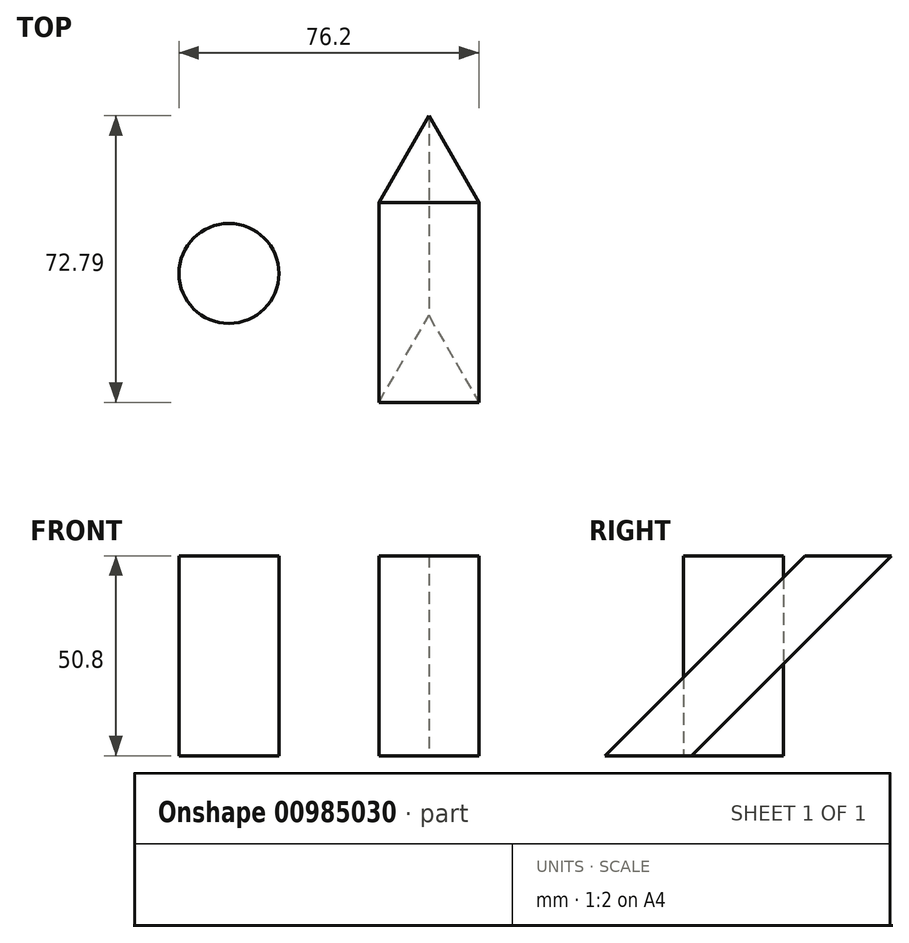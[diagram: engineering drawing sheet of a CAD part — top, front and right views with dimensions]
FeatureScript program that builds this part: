
annotation { "Feature Type Name" : "Feature", "Feature Type Description" : "" }
export const myFeature = defineFeature(function(context is Context, id is Id, definition is map)
    precondition{}
    {
        {
            var Q0;
            Q0=qCreatedBy(makeId("Top.planeOp"),FACE);
            var sketch = newSketch(context, id + "F0", { "sketchPlane" : qUnion([Q0])});
            skCircle(sketch, "E0", {"center": v(-25.4, 0) * mm, "radius": 12.7 * mm});
            skPoint(sketch, "E1.middle", {"position": v(25.4, -25.4) * mm});
            skCircle(sketch, "E2.cCircle", {"center": v(25.4, -25.4) * mm, "radius": 7.33 * mm, "construction": true});
            skLineSegment(sketch, "E2.0", {"start": v(38.1, -32.73) * mm, "end": v(12.7, -32.73) * mm});
            skLineSegment(sketch, "E2.1", {"start": v(12.7, -32.73) * mm, "end": v(25.4, -10.74) * mm});
            skLineSegment(sketch, "E2.2", {"start": v(25.4, -10.74) * mm, "end": v(38.1, -32.73) * mm});
            skPoint(sketch, "E2.0.midPoint", {"position": v(25.4, -32.73) * mm});
            skSolve(sketch);
        }
        {
            var Q0;
            Q0=qCreatedBy(makeId("Top.planeOp"),FACE);
            cPlane(context, id + "F1", {"entities" : qUnion([Q0]), "cplaneType" : CPlaneType.OFFSET, "offset" : 50.8 * mm, "width" : 152.4 * mm, "height" : 152.4 * mm});
        }
        {
            var Q0;
            Q0=qCreatedBy(id+"F1.planeOp",FACE);
            var sketch = newSketch(context, id + "F2", { "sketchPlane" : qUnion([Q0])});
            skPoint(sketch, "E3.middle", {"position": v(25.4, 25.4) * mm});
            skCircle(sketch, "E4.cCircle", {"center": v(25.4, 25.4) * mm, "radius": 7.33 * mm, "construction": true});
            skLineSegment(sketch, "E4.0", {"start": v(38.1, 18.07) * mm, "end": v(12.7, 18.07) * mm});
            skLineSegment(sketch, "E4.1", {"start": v(12.7, 18.07) * mm, "end": v(25.4, 40.06) * mm});
            skLineSegment(sketch, "E4.2", {"start": v(25.4, 40.06) * mm, "end": v(38.1, 18.07) * mm});
            skPoint(sketch, "E4.0.midPoint", {"position": v(25.4, 18.07) * mm});
            skSolve(sketch);
        }
        {
            var Q0;
            Q0=makeQuery(id+"F0.imprint","IMPRINT",FACE,{"disambiguationData":[TD([[makeQuery(id+"F0.imprint","IMPRINT",EDGE,{"derivedFrom":sQuery(id+"F0.wireOp",EDGE,"E0")}),1.0]])]});
            extrude(context, id + "F3", {"entities" : qUnion([Q0]), "depth" : 50.8 * mm, "offsetDistance" : 25.4 * mm});
        }
        {
            var Q0;
            Q0=makeQuery(id+"F2.imprint","IMPRINT",FACE,{"disambiguationData":[TD([[makeQuery(id+"F2.imprint","IMPRINT",EDGE,{"derivedFrom":sQuery(id+"F2.wireOp",EDGE,"E4.0")}),-1.0]])]});
            var Q1;
            Q1=makeQuery(id+"F0.imprint","IMPRINT",FACE,{"disambiguationData":[TD([[makeQuery(id+"F0.imprint","IMPRINT",EDGE,{"derivedFrom":sQuery(id+"F0.wireOp",EDGE,"E2.0")}),-1.0]])]});
            loft(context, id + "F4", {"sheetProfilesArray" : [{ "sheetProfileEntities" : qUnion([Q0]) }, { "sheetProfileEntities" : qUnion([Q1]) }]});
        }
    });
